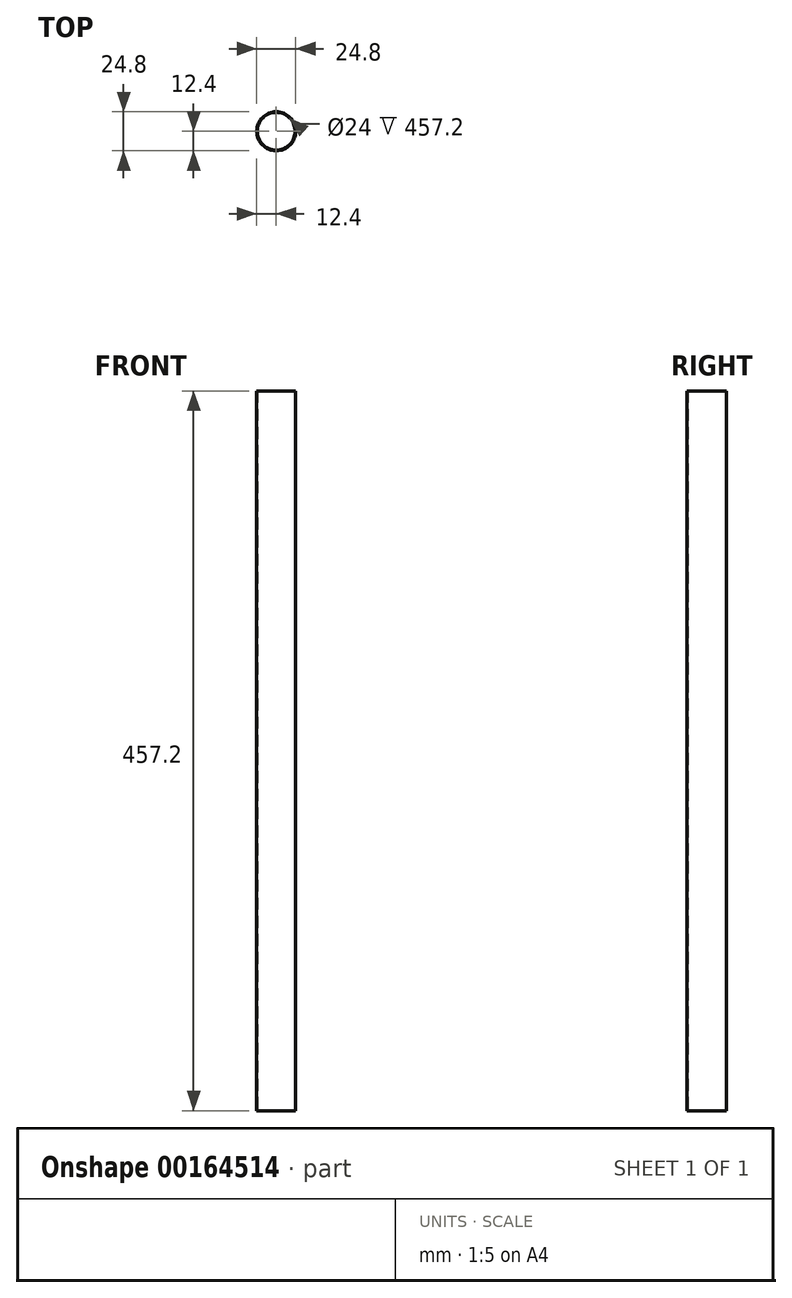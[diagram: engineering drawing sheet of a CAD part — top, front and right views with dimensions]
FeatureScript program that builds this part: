
annotation { "Feature Type Name" : "Feature", "Feature Type Description" : "" }
export const myFeature = defineFeature(function(context is Context, id is Id, definition is map)
    precondition{}
    {
        {
            var Q0;
            Q0=qCreatedBy(makeId("Top.planeOp"),FACE);
            var sketch = newSketch(context, id + "F0", { "sketchPlane" : qUnion([Q0])});
            skCircle(sketch, "E0", {"center": v(0, 0) * mm, "radius": 12 * mm});
            skCircle(sketch, "E1", {"center": v(0, 0) * mm, "radius": 12.4 * mm});
            skSolve(sketch);
        }
        {
            var Q0;
            Q0=makeQuery(id+"F0.imprint","IMPRINT",FACE,{"disambiguationData":[TD([[makeQuery(id+"F0.imprint","IMPRINT",EDGE,{"derivedFrom":sQuery(id+"F0.wireOp",EDGE,"E0")}),-1.0]])]});
            extrude(context, id + "F1", {"entities" : qUnion([Q0]), "depth" : 457.2 * mm});
        }
    });
